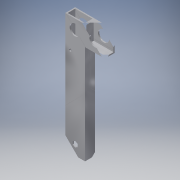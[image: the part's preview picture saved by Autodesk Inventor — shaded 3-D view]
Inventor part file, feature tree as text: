
AUTODESK INVENTOR PART (.ipt)
format: ipt  version: 2016 (Build 200138000, 138)  size: 169,984 bytes
history: native  units: in
note: dims shown in document units (in); Inventor stores cm internally (conversion verified against a paired STEP export)
features: extrude x6, sketch x6
ambient origin geometry x8: Origin, YZ Plane, XZ Plane, XY Plane, X Axis, Y Axis, Z Axis, Center Point
bodies: Solid1 (feature_tree)
feature tree (12):
  extrude  "Extrusion1"  Depth=1.0in
  extrude  "Extrusion2"  Depth=0.1253in
  extrude  "Extrusion3"  Depth=0.125in
  extrude  "Extrusion4"  Depth=2.0in
  extrude  "Extrusion5"  Depth=0.125in
  extrude  "Extrusion6"  Depth=1.0in
  sketch  "Sketch1"  dims[d0=2.0in d1=1.0in]
  sketch  "Sketch2"  dims[d2=0.125in d3=0.1253in]
  sketch  "Sketch3"  dims[d4=0.125in d5=0.125in]
  sketch  "Sketch4"  dims[d6=12.0in d7=0.0in d8=2.0in]
  sketch  "Sketch5"  dims[d9=0.125in d10=0.125in]
  sketch  "Sketch6"  dims[d11=2.0in d12=0.0in d13=1.0in d14=1.125in d15=2.0in d16=0.0in d17=1.0in d18=1.125in d19=2.0in d20=0.0in d21=1.0in d22=1.125in d23=1.0in d24=1.0in d25=0.0in d26=1.0in d27=1.0in d28=0.75in d29=0.5in d30=1.0in d31=0.0in d32=0.2656in d33=3.0in d34=0.5in]
